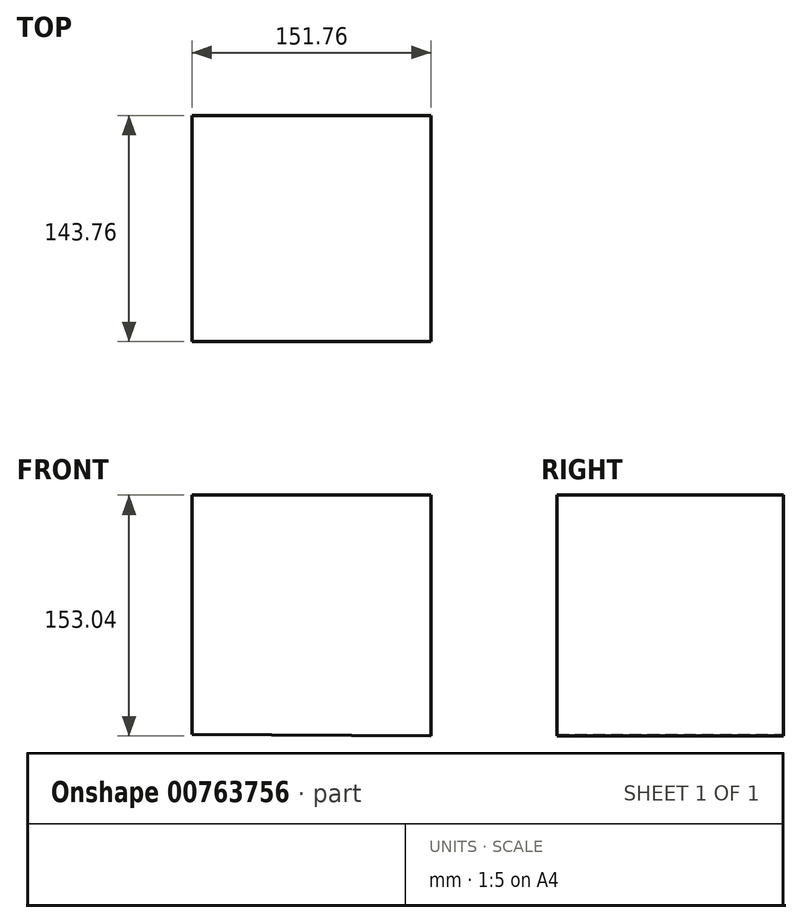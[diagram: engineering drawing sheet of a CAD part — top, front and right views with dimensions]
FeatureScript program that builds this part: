
annotation { "Feature Type Name" : "Feature", "Feature Type Description" : "" }
export const myFeature = defineFeature(function(context is Context, id is Id, definition is map)
    precondition{}
    {
        {
            var Q0;
            Q0=qCreatedBy(makeId("Front.planeOp"),FACE);
            var sketch = newSketch(context, id + "F0", { "sketchPlane" : qUnion([Q0])});
            skLineSegment(sketch, "E0", {"start": v(-75.88, -75.67) * mm, "end": v(-75.88, 76.3) * mm});
            skLineSegment(sketch, "E1", {"start": v(-75.88, 76.3) * mm, "end": v(75.88, 76.3) * mm});
            skLineSegment(sketch, "E2", {"start": v(75.88, 76.3) * mm, "end": v(75.88, -76.73) * mm});
            skLineSegment(sketch, "E3", {"start": v(75.88, -76.73) * mm, "end": v(-75.88, -75.67) * mm});
            skSolve(sketch);
        }
        {
            var Q0;
            Q0=makeQuery(id+"F0.imprint","IMPRINT",FACE,{"disambiguationData":[TD([[makeQuery(id+"F0.imprint","IMPRINT",EDGE,{"derivedFrom":sQuery(id+"F0.wireOp",EDGE,"E0")}),-1.0]])]});
            extrude(context, id + "F1", {"entities" : qUnion([Q0]), "depth" : 143.76 * mm, "offsetDistance" : 25.4 * mm});
        }
    });
